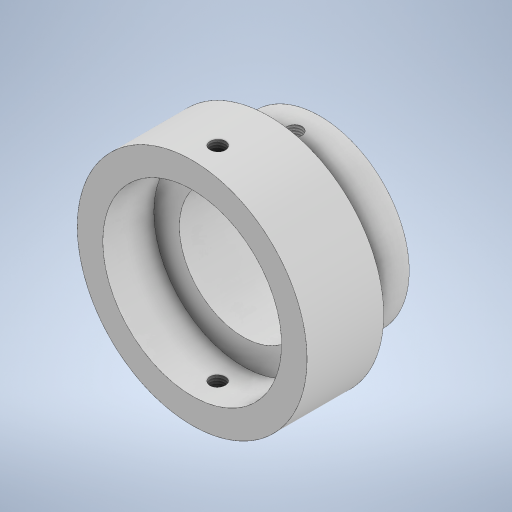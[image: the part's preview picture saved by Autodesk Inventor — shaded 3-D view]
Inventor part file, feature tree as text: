
AUTODESK INVENTOR PART (.ipt)
format: ipt  version: 2023 (Build 270158000, 158)  size: 307,200 bytes
history: native  units: mm
features: thread x2, sketch x2, revolve x1, extrude x1
ambient origin geometry x8: Origin, YZ Plane, XZ Plane, XY Plane, X Axis, Y Axis, Z Axis, Center Point
bodies: Body1 (feature_tree)
feature tree (6):
  revolve  "Вращение1"
  extrude  "Выдавливание3"  Depth=10.0mm
  thread  "Резьба1"
  thread  "Резьба2"
  sketch  "Эскиз1"
  sketch  "Эскиз4"
